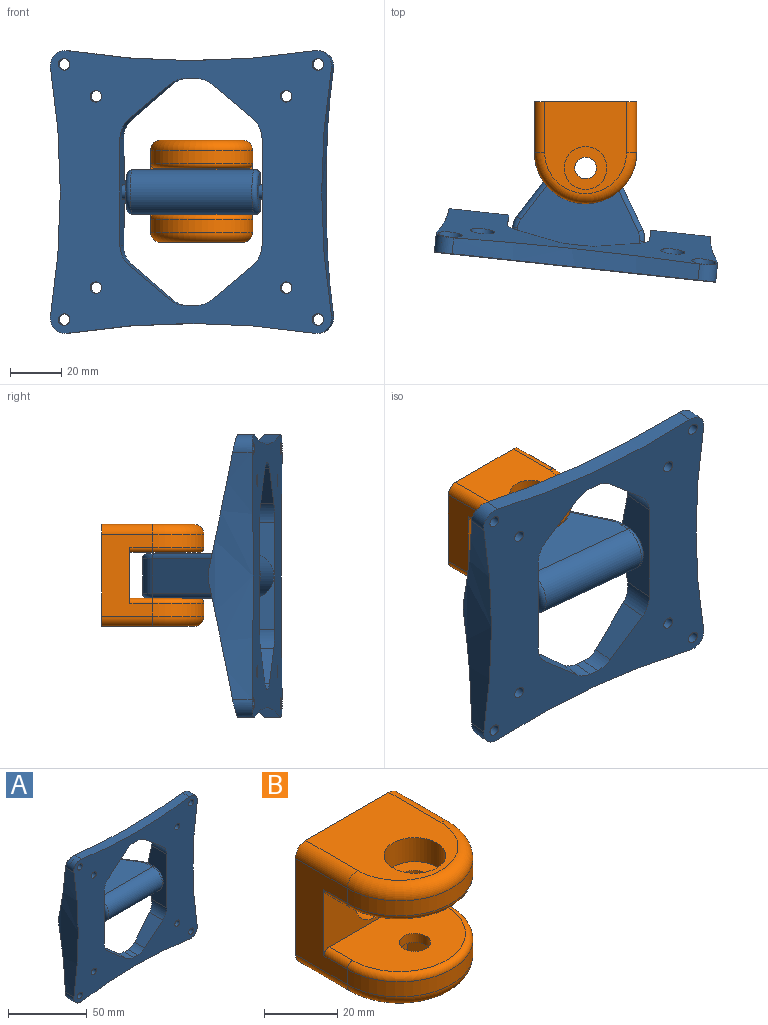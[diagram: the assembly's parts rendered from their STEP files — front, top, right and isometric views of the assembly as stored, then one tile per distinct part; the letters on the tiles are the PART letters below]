
ASSEMBLY  parts=2 mates=1
PART A: 94 faces, bbox 111.2x50.9x111.2 mm
  f0: cylinder r=4.75mm len=9.5mm, axis (0,-1,0), area 181.3mm2, adj f61,f87
  f1: cylinder r=4.75mm len=9.5mm, axis (0,-1,0), area 179.2mm2, adj f63,f86
  f2: cylinder r=4.75mm len=9.5mm, axis (0,-1,0), area 181.3mm2, adj f61,f85
  f3: cylinder r=4.75mm len=9.5mm, axis (0,-1,0), area 179.2mm2, adj f63,f84
  f4: cylinder r=4.75mm len=9.5mm, axis (0,-1,0), area 102mm2, adj f61,f83
  f5: cylinder r=4.75mm len=9.5mm, axis (0,-1,0), area 99.9mm2, adj f63,f82
  f6: cylinder r=4.75mm len=9.5mm, axis (0,-1,0), area 102mm2, adj f61,f81
  f7: cylinder r=4.75mm len=9.5mm, axis (0,-1,0), area 99.9mm2, adj f63,f80
  f8: cylinder r=2.25mm len=4.5mm, axis (0,-1,0), area 56.5mm2, adj f51,f87
  f9: cylinder r=2.25mm len=4.5mm, axis (0,-1,0), area 56.5mm2, adj f51,f86
  f10: cylinder r=2.25mm len=4.5mm, axis (0,-1,0), area 56.5mm2, adj f51,f85
  f11: cylinder r=2.25mm len=4.5mm, axis (0,-1,0), area 56.5mm2, adj f51,f84
  f12: cylinder r=2.25mm len=4.5mm, axis (0,-1,0), area 56.5mm2, adj f51,f83
  f13: cylinder r=2.25mm len=4.5mm, axis (0,-1,0), area 56.5mm2, adj f51,f82
  f14: cylinder r=2.25mm len=4.5mm, axis (0,-1,0), area 56.5mm2, adj f51,f81
  f15: cylinder r=2.25mm len=4.5mm, axis (0,-1,0), area 56.5mm2, adj f51,f80
  f16: cylinder r=8.75mm len=48mm, axis (-1,0,0), area 1319.5mm2, adj f42,f45,f49,f50
  f17: cylinder r=2.75mm len=5.5mm, axis (-1,0,0), area 34.6mm2, adj f48,f72
  f18: cylinder r=2.75mm len=5.5mm, axis (-1,0,0), area 34.6mm2, adj f47,f64
  f19: cylinder r=4.3mm len=17.5mm, axis (0,0,-1), area 472.8mm2, adj f42,f45
  f20: plane 13.5x0.36mm, normal (0,1,0), area 4.9mm2, adj f21,f23,f27,f28
  f21: cylinder r=9.5mm len=13.5mm, axis (0,0,-1), area 130.9mm2, adj f20,f22,f26,f31
  f22: torus R=7.5mm, axis (0,0,1), area 28.1mm2, adj f21,f27,f30,f42
  f23: cylinder r=9.5mm len=13.5mm, axis (0,0,-1), area 130.9mm2, adj f20,f24,f25,f33
  f24: torus R=7.5mm, axis (0,0,-1), area 28.1mm2, adj f23,f28,f29,f45
  f25: torus R=7.5mm, axis (0,0,-1), area 28.1mm2, adj f23,f27,f34,f42
  f26: torus R=7.5mm, axis (0,0,1), area 28.1mm2, adj f21,f28,f32,f45
  f27: cylinder r=2mm len=2mm, axis (-1,0,0), area 1.1mm2, adj f20,f22,f25,f42
  f28: cylinder r=2mm len=2mm, axis (1,0,0), area 1.1mm2, adj f20,f24,f26,f45
  f29: cylinder r=2mm len=28.14mm, axis (0.52,0.85,0), area 99.7mm2, adj f24,f33,f39,f40,f45
  f30: cylinder r=2mm len=28.14mm, axis (-0.52,0.85,0), area 99.7mm2, adj f22,f31,f36,f37,f42
  f31: plane 26.63x16.32mm, normal (0.85,0.52,0), area 421.7mm2, adj f21,f30,f32,f36
  f32: cylinder r=2mm len=28.14mm, axis (-0.52,0.85,0), area 99.7mm2, adj f26,f31,f36,f45,f46
  f33: plane 26.63x16.32mm, normal (-0.85,0.52,0), area 421.7mm2, adj f23,f29,f34,f39
  f34: cylinder r=2mm len=28.14mm, axis (0.52,0.85,0), area 99.7mm2, adj f25,f33,f39,f42,f43
  f35: cylinder r=2mm len=5.01mm, axis (0,-1,0), area 12.9mm2, adj f36,f37,f42,f47,f49
  f36: cylinder r=9.5mm len=14.32mm, axis (0,0,-1), area 75.9mm2, adj f30,f31,f32,f35,f37,f44,f46,f47
  f37: torus R=7.5mm, axis (0,0,1), area 12.6mm2, adj f30,f35,f36,f42
  f38: cylinder r=2mm len=5.01mm, axis (0,-1,0), area 12.9mm2, adj f39,f40,f45,f48,f50
  f39: cylinder r=9.5mm len=14.32mm, axis (0,0,-1), area 71.8mm2, adj f29,f33,f34,f38,f40,f41,f43,f48
  f40: torus R=7.5mm, axis (0,0,-1), area 12.6mm2, adj f29,f38,f39,f45
  f41: cylinder r=2mm len=5.01mm, axis (0,-1,0), area 15.6mm2, adj f39,f42,f43,f48,f50
  f42: plane 48x38.25mm, normal (0,0,1), area 1143.4mm2, adj f16,f19,f22,f25,f27,f30,f34,f35
  f43: torus R=7.5mm, axis (0,0,-1), area 12.6mm2, adj f34,f39,f41,f42
  f44: cylinder r=2mm len=5.01mm, axis (0,-1,0), area 15.6mm2, adj f36,f45,f46,f47,f49
  f45: plane 48x38.25mm, normal (0,0,-1), area 1143.4mm2, adj f16,f19,f24,f26,f28,f29,f32,f38
  f46: torus R=7.5mm, axis (0,0,1), area 12.6mm2, adj f32,f36,f44,f45
  f47: plane 13.5x10.87mm, normal (1,0,0), area 103.4mm2, adj f18,f35,f36,f44,f49
  f48: plane 13.5x10.87mm, normal (-1,0,0), area 103.4mm2, adj f17,f38,f39,f41,f50
  f49: torus R=6.75mm, axis (1,0,0), area 79.2mm2, adj f16,f35,f44,f47
  f50: torus R=6.75mm, axis (-1,0,0), area 79.2mm2, adj f16,f38,f41,f48
  f51: plane 110.82x110.82mm, normal (0,-1,0), area 6990.4mm2, adj f8,f9,f10,f11,f12,f13,f14,f15
  f52: plane 23.51x4.79mm, normal (0,1,0), area 112.7mm2, adj f57,f61,f63,f64
  f53: cylinder r=308mm len=96.94mm, axis (0,-1,0), area 661mm2, adj f51,f54,f58,f63
  f54: cylinder r=6mm len=7.71mm, axis (0,-1,0), area 76.2mm2, adj f51,f53,f57,f63
  f55: cylinder r=6mm len=7.71mm, axis (0,-1,0), area 76.2mm2, adj f51,f56,f60,f61
  f56: cylinder r=308mm len=96.94mm, axis (0,-1,0), area 1250.3mm2, adj f51,f55,f58,f61,f62,f63
  f57: cylinder r=308mm len=96.94mm, axis (0,-1,0), area 1250.3mm2, adj f51,f52,f54,f59,f61,f63
  f58: cylinder r=6mm len=7.71mm, axis (0,-1,0), area 76.2mm2, adj f51,f53,f56,f63
  f59: cylinder r=6mm len=7.71mm, axis (0,-1,0), area 76.2mm2, adj f51,f57,f60,f61
  f60: cylinder r=308mm len=96.94mm, axis (0,-1,0), area 661mm2, adj f51,f55,f59,f61
  f61: plane 111.25x53.44mm, normal (0,0.98,-0.21), area 3233.3mm2, adj f0,f2,f4,f6,f52,f55,f56,f57
  f62: plane 23.51x4.79mm, normal (0,1,0), area 112.7mm2, adj f56,f61,f63,f72
  f63: plane 111.25x53.44mm, normal (0,0.98,0.21), area 3233.3mm2, adj f1,f3,f5,f7,f52,f53,f54,f56
  f64: plane 41.71x17.5mm, normal (-1,0,0), area 633.8mm2, adj f18,f51,f52,f61,f63,f65,f79
  f65: cylinder r=10mm len=13.58mm, axis (0,-1,0), area 111mm2, adj f51,f61,f64,f66
  f66: plane 16.16x13.64mm, normal (-0.65,0,0.76), area 222.1mm2, adj f51,f61,f65,f67
  f67: cylinder r=10mm len=9.05mm, axis (0,-1,0), area 61.7mm2, adj f51,f61,f66,f68
  f68: plane 8.55x3.69mm, normal (0,0,1), area 31.5mm2, adj f51,f61,f67,f69
  f69: cylinder r=10mm len=9.05mm, axis (0,-1,0), area 61.7mm2, adj f51,f61,f68,f70
  f70: plane 16.16x13.64mm, normal (0.65,0,0.76), area 222.1mm2, adj f51,f61,f69,f71
  f71: cylinder r=10mm len=13.58mm, axis (0,-1,0), area 111mm2, adj f51,f61,f70,f72
  f72: plane 41.71x17.5mm, normal (1,0,0), area 633.8mm2, adj f17,f51,f61,f62,f63,f71,f73
  f73: cylinder r=10mm len=13.58mm, axis (0,-1,0), area 111mm2, adj f51,f63,f72,f74
  f74: plane 16.16x13.64mm, normal (0.65,0,-0.76), area 222.1mm2, adj f51,f63,f73,f75
  f75: cylinder r=10mm len=9.05mm, axis (0,-1,0), area 61.7mm2, adj f51,f63,f74,f76
  f76: plane 8.55x3.69mm, normal (0,0,-1), area 31.5mm2, adj f51,f63,f75,f77
  f77: cylinder r=10mm len=9.05mm, axis (0,-1,0), area 61.7mm2, adj f51,f63,f76,f78
  f78: plane 16.16x13.64mm, normal (-0.65,0,-0.76), area 222.1mm2, adj f51,f63,f77,f79
  f79: cylinder r=10mm len=13.58mm, axis (0,-1,0), area 111mm2, adj f51,f63,f64,f78
  f80: plane 9.5x9.5mm, normal (0,1,0), area 55mm2, adj f7,f15
  f81: plane 9.5x9.5mm, normal (0,1,0), area 55mm2, adj f6,f14
  f82: plane 9.5x9.5mm, normal (0,1,0), area 55mm2, adj f5,f13
  f83: plane 9.5x9.5mm, normal (0,1,0), area 55mm2, adj f4,f12
  f84: plane 9.5x9.5mm, normal (0,1,0), area 55mm2, adj f3,f11
  f85: plane 9.5x9.5mm, normal (0,1,0), area 55mm2, adj f2,f10
  f86: plane 9.5x9.5mm, normal (0,1,0), area 55mm2, adj f1,f9
  f87: plane 9.5x9.5mm, normal (0,1,0), area 55mm2, adj f0,f8
  f88: cylinder r=2.75mm len=5.5mm, axis (-1,0,0), area 48.8mm2, adj f89,f90
  f89: plane 5.5x5.5mm, normal (1,0,0), area 23.8mm2, adj f88
  f90: plane 5.5x5.5mm, normal (-1,0,0), area 23.8mm2, adj f88
  f91: cylinder r=2.75mm len=5.5mm, axis (-1,0,0), area 48.8mm2, adj f92,f93
  f92: plane 5.5x5.5mm, normal (-1,0,0), area 23.8mm2, adj f91
  f93: plane 5.5x5.5mm, normal (1,0,0), area 23.8mm2, adj f91
PART B: 36 faces, bbox 43.3x41.6x40 mm
  f0: cylinder r=8mm len=16mm, axis (0,1,0), area 402.1mm2, adj f24,f26
  f1: cylinder r=4.5mm len=9mm, axis (0,1,0), area 84.8mm2, adj f24,f30
  f2: cylinder r=8.4mm len=16.8mm, axis (0,0,1), area 422.2mm2, adj f23,f32
  f3: cylinder r=4.25mm len=8.5mm, axis (0,0,-1), area 80.1mm2, adj f23,f25
  f4: cylinder r=4.25mm len=8.5mm, axis (0,0,-1), area 80.1mm2, adj f10,f22
  f5: torus R=18mm, axis (0,0,1), area 190.2mm2, adj f6,f9,f10,f11
  f6: cylinder r=20mm len=40mm, axis (0,0,-1), area 314.2mm2, adj f5,f12,f14,f28
  f7: torus R=18mm, axis (0,0,-1), area 190.2mm2, adj f8,f13,f15,f25
  f8: cylinder r=20mm len=40mm, axis (0,0,-1), area 314.2mm2, adj f7,f12,f14,f27
  f9: cylinder r=2mm len=9mm, axis (0,1,0), area 28.3mm2, adj f5,f10,f14,f26
  f10: plane 36x27mm, normal (0,0,1), area 776.2mm2, adj f4,f5,f9,f11,f26
  f11: cylinder r=2mm len=9mm, axis (0,1,0), area 28.3mm2, adj f5,f10,f12,f26
  f12: plane 32x20mm, normal (-1,0,0), area 442mm2, adj f6,f8,f11,f15,f26,f30,f33,f34
  f13: cylinder r=2mm len=9mm, axis (0,1,0), area 28.3mm2, adj f7,f14,f25,f26
  f14: plane 32x20mm, normal (1,0,0), area 442mm2, adj f6,f8,f9,f13,f26,f29,f30,f31
  f15: cylinder r=2mm len=9mm, axis (0,1,0), area 28.3mm2, adj f7,f12,f25,f26
  f16: plane 8x6.5mm, normal (-0.87,-0.5,0), area 60mm2, adj f17,f21,f22,f35
  f17: plane 8x7.51mm, normal (0,-1,0), area 60mm2, adj f16,f18,f22,f35
  f18: plane 8x6.5mm, normal (0.87,-0.5,0), area 60mm2, adj f17,f19,f22,f35
  f19: plane 8x6.5mm, normal (0.87,0.5,0), area 60mm2, adj f18,f20,f22,f35
  f20: plane 8x7.51mm, normal (0,1,0), area 60mm2, adj f19,f21,f22,f35
  f21: plane 8x6.5mm, normal (-0.87,0.5,0), area 60mm2, adj f16,f20,f22,f35
  f22: plane 15.01x13mm, normal (0,0,-1), area 89.6mm2, adj f4,f16,f17,f18,f19,f20,f21
  f23: plane 16.8x16.8mm, normal (0,0,1), area 164.9mm2, adj f2,f3
  f24: plane 16x16mm, normal (0,-1,0), area 137.4mm2, adj f0,f1
  f25: plane 36x27mm, normal (0,0,-1), area 776.2mm2, adj f3,f7,f13,f15,f26
  f26: plane 40x22mm, normal (0,-1,0), area 522.4mm2, adj f0,f9,f10,f11,f12,f13,f14,f15
  f27: torus R=16mm, axis (0,0,1), area 366.1mm2, adj f8,f31,f32,f33
  f28: torus R=16mm, axis (0,0,-1), area 366.1mm2, adj f6,f29,f34,f35
  f29: cylinder r=4mm len=20mm, axis (0,1,0), area 125.7mm2, adj f14,f28,f30,f35
  f30: plane 40x40mm, normal (0,1,0), area 1522.6mm2, adj f1,f12,f14,f29,f31,f32,f33,f34
  f31: cylinder r=4mm len=20mm, axis (0,1,0), area 125.7mm2, adj f14,f27,f30,f32
  f32: plane 36x32mm, normal (0,0,1), area 820.5mm2, adj f2,f27,f30,f31,f33
  f33: cylinder r=4mm len=20mm, axis (0,1,0), area 125.7mm2, adj f12,f27,f30,f32
  f34: cylinder r=4mm len=20mm, axis (0,1,0), area 125.7mm2, adj f12,f28,f30,f35
  f35: plane 36x32mm, normal (0,0,-1), area 895.8mm2, adj f16,f17,f18,f19,f20,f21,f28,f29
PLACE A rot(axis=(0,0,-1),6.1deg) t=(1.37,33.27,2.33)mm
PLACE B t=(-1.39,33.42,2.58)mm fixed
MATE revolute A.f19 <-> B.f2  axis (0,0,-1) through (-1.39,7.42,-6.42)mm
